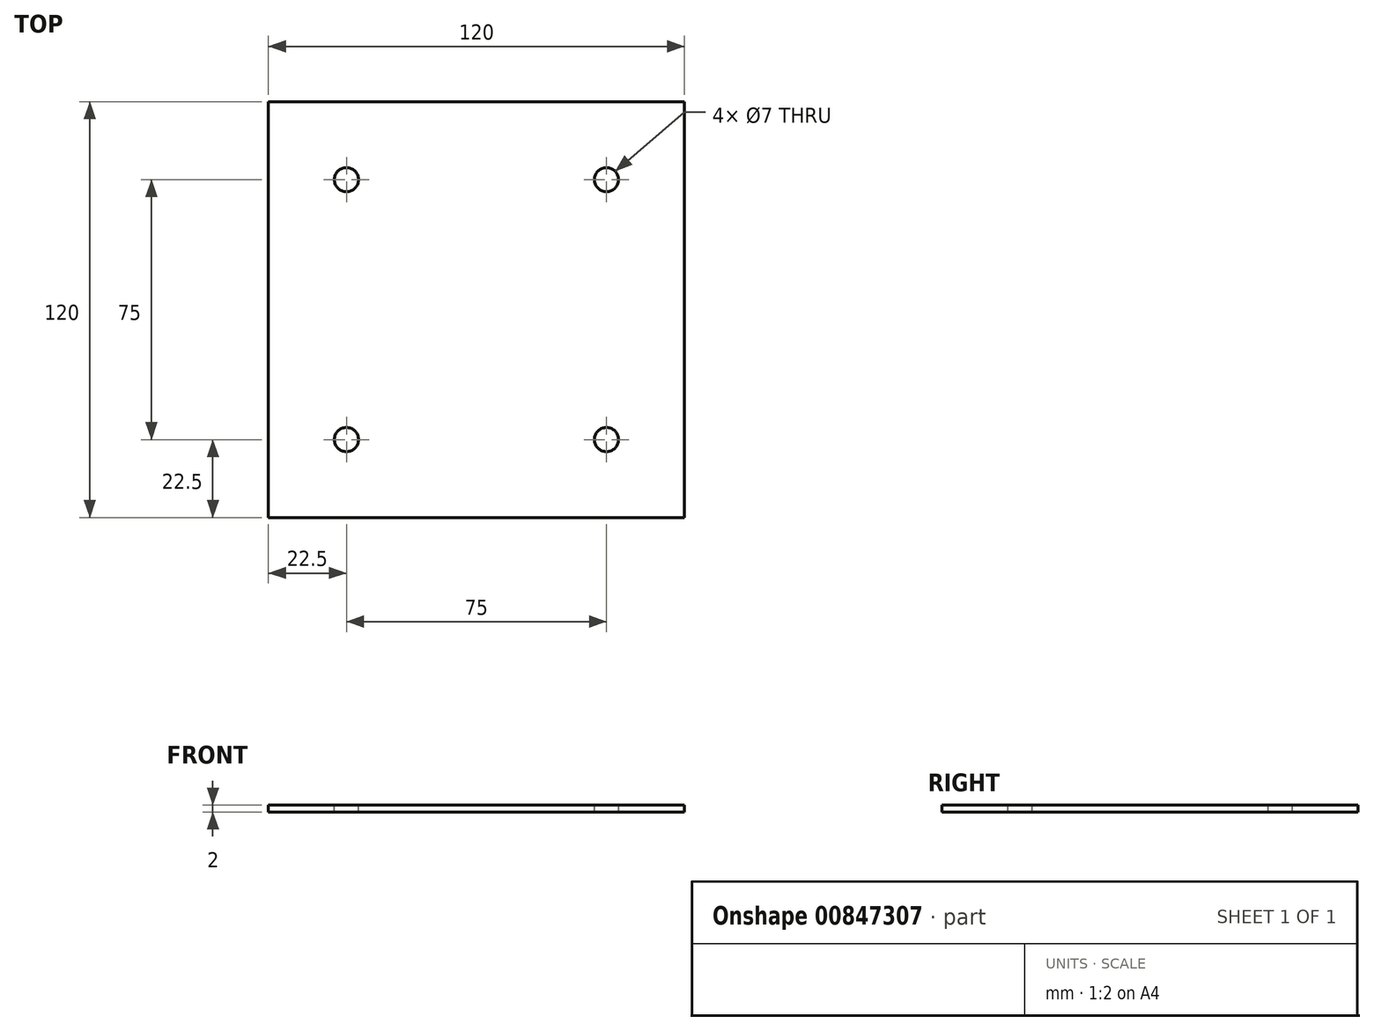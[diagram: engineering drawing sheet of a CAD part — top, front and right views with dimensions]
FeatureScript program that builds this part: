
annotation { "Feature Type Name" : "Feature", "Feature Type Description" : "" }
export const myFeature = defineFeature(function(context is Context, id is Id, definition is map)
    precondition{}
    {
        {
            var Q0;
            Q0=qCreatedBy(makeId("Top.planeOp"),FACE);
            var sketch = newSketch(context, id + "F0", { "sketchPlane" : qUnion([Q0])});
            skLineSegment(sketch, "E0.bottom", {"start": v(60, -60) * mm, "end": v(-60, -60) * mm});
            skLineSegment(sketch, "E0.top", {"start": v(60, 60) * mm, "end": v(-60, 60) * mm});
            skLineSegment(sketch, "E0.left", {"start": v(60, -60) * mm, "end": v(60, 60) * mm});
            skLineSegment(sketch, "E0.right", {"start": v(-60, -60) * mm, "end": v(-60, 60) * mm});
            skPoint(sketch, "E0.middle", {"position": v(0, 0) * mm});
            skSolve(sketch);
        }
        {
            var Q0;
            Q0 = qSketchRegion(id + "F0", true);
            extrude(context, id + "F1", {"entities" : qUnion([Q0]), "depth" : 2 * mm, "offsetDistance" : 25 * mm});
        }
        {
            var Q0;
            Q0=makeQuery(id+"F1.opExtrude","CAP_FACE",FACE,{"disambiguationData":[OSD([sQuery(id+"F0.wireOp",EDGE,"E0.bottom"),sQuery(id+"F0.wireOp",EDGE,"E0.top"),sQuery(id+"F0.wireOp",EDGE,"E0.left"),sQuery(id+"F0.wireOp",EDGE,"E0.right")])],"isStart":false});
            var sketch = newSketch(context, id + "F2", { "sketchPlane" : qUnion([Q0])});
            skPoint(sketch, "E1", {"position": v(-37.5, 37.5) * mm});
            skPoint(sketch, "E2", {"position": v(37.5, 37.5) * mm});
            skPoint(sketch, "E3", {"position": v(37.5, -37.5) * mm});
            skPoint(sketch, "E4", {"position": v(-37.5, -37.5) * mm});
            skCircle(sketch, "E5", {"center": v(-37.5, 37.5) * mm, "radius": 3.5 * mm});
            skCircle(sketch, "E6", {"center": v(37.5, 37.5) * mm, "radius": 3.5 * mm});
            skCircle(sketch, "E7", {"center": v(-37.5, -37.5) * mm, "radius": 3.5 * mm});
            skCircle(sketch, "E8", {"center": v(37.5, -37.5) * mm, "radius": 3.5 * mm});
            skSolve(sketch);
        }
        {
            var Q0;
            Q0 = qSketchRegion(id + "F2", true);
            extrude(context, id + "F3", {"entities" : qUnion([Q0]), "operationType" : NewBodyOperationType.REMOVE, "endBound" : BoundingType.THROUGH_ALL, "oppositeDirection" : true, "depth" : 25 * mm, "offsetDistance" : 25 * mm});
        }
    });
